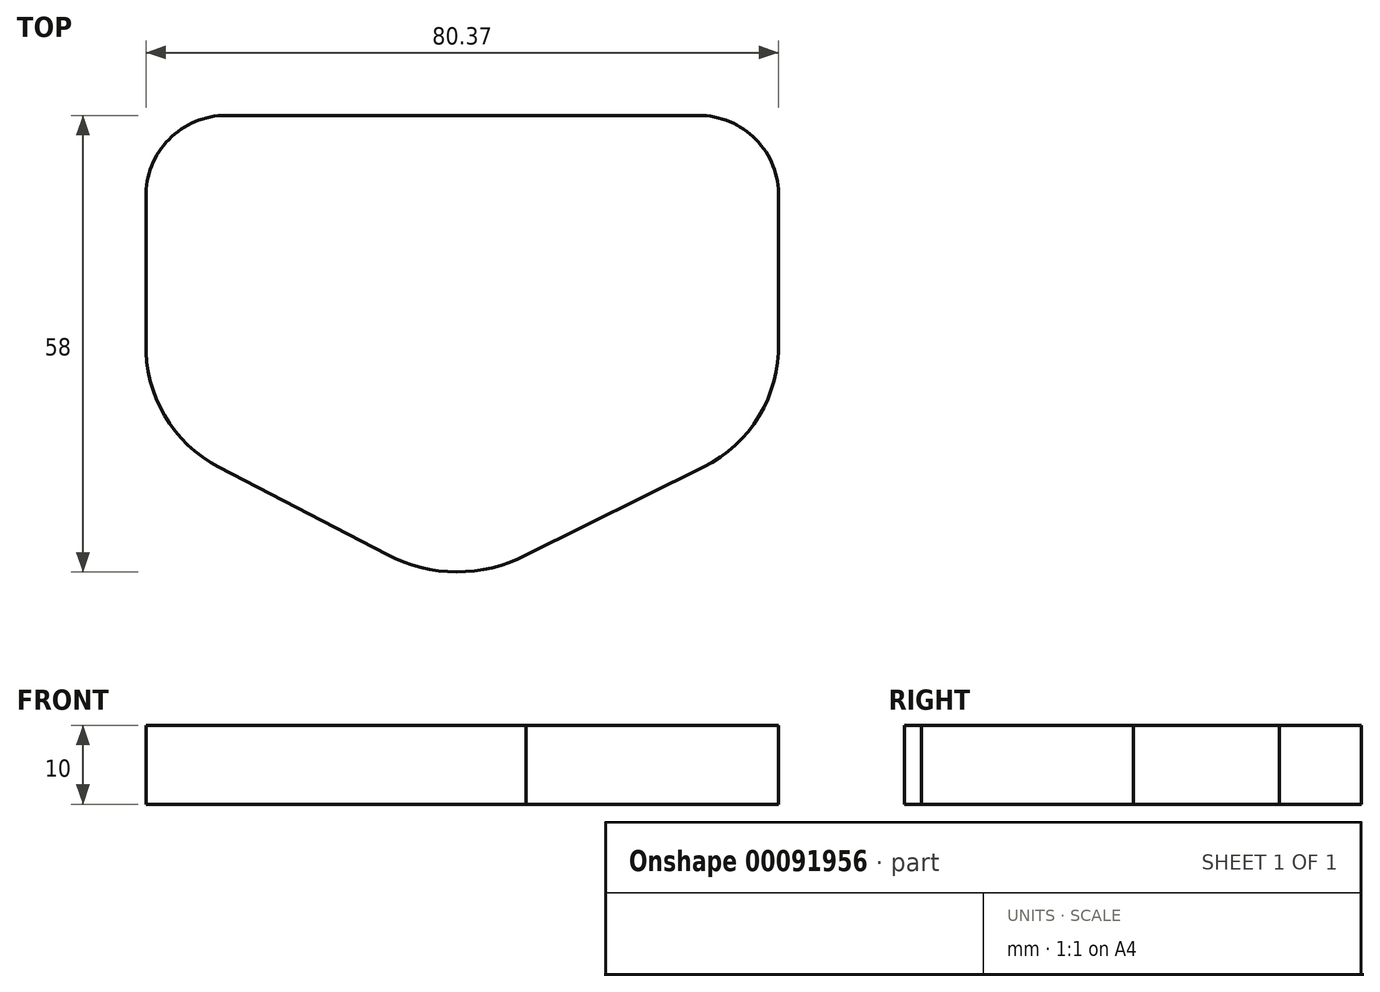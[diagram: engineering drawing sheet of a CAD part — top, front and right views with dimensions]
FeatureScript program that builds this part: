
annotation { "Feature Type Name" : "Feature", "Feature Type Description" : "" }
export const myFeature = defineFeature(function(context is Context, id is Id, definition is map)
    precondition{}
    {
        {
            var Q0;
            Q0=qCreatedBy(makeId("Top.planeOp"),FACE);
            var sketch = newSketch(context, id + "F0", { "sketchPlane" : qUnion([Q0])});
            skLineSegment(sketch, "E0.bottom", {"start": v(40, -20) * mm, "end": v(-40, -20) * mm});
            skLineSegment(sketch, "E0.top", {"start": v(30.2, 20) * mm, "end": v(-29.85, 20) * mm});
            skPoint(sketch, "E0.middle", {"position": v(0, 0) * mm});
            skPoint(sketch, "E1.visualSharp", {"position": v(-40, 20) * mm});
            skArc(sketch, "E1.filletArc", {"start": v(-29.85, 20) * mm, "mid": v(-37.1, 16.95) * mm, "end": v(-40, 9.63) * mm});
            skPoint(sketch, "E2.visualSharp", {"position": v(40, 20) * mm});
            skArc(sketch, "E2.filletArc", {"start": v(40.35, 9.63) * mm, "mid": v(37.45, 16.95) * mm, "end": v(30.2, 20) * mm});
            skPoint(sketch, "E3.visualSharp", {"position": v(0, -40.97) * mm});
            skArc(sketch, "E3.filletArc", {"start": v(-9.4, -35.78) * mm, "mid": v(-0.57, -38) * mm, "end": v(8.28, -35.87) * mm});
            skLineSegment(sketch, "E4", {"start": v(-30.76, -24.68) * mm, "end": v(-9.4, -35.78) * mm});
            skLineSegment(sketch, "E5", {"start": v(8.28, -35.87) * mm, "end": v(30.82, -24.68) * mm});
            skArc(sketch, "E6", {"start": v(-40, -8.91) * mm, "mid": v(-37.66, -18.13) * mm, "end": v(-30.76, -24.68) * mm});
            skArc(sketch, "E7", {"start": v(30.82, -24.68) * mm, "mid": v(37.88, -18.18) * mm, "end": v(40.35, -8.91) * mm});
            skLineSegment(sketch, "E8", {"start": v(40.35, -8.91) * mm, "end": v(40.35, 9.63) * mm});
            skLineSegment(sketch, "E9", {"start": v(-40, -8.91) * mm, "end": v(-40, 9.63) * mm});
            skSolve(sketch);
        }
        {
            var Q0;
            Q0=makeQuery(id+"F0.imprint","IMPRINT",FACE,{"disambiguationData":[TD([[makeQuery(id+"F0.imprint","IMPRINT",EDGE,{"derivedFrom":sQuery(id+"F0.wireOp",EDGE,"E3.filletArc")}),1.0]])]});
            var Q1;
            Q1=makeQuery(id+"F0.imprint","IMPRINT",FACE,{"disambiguationData":[TD([[makeQuery(id+"F0.imprint","IMPRINT",EDGE,{"derivedFrom":sQuery(id+"F0.wireOp",EDGE,"E0.top")}),1.0]])]});
            extrude(context, id + "F1", {"entities" : qUnion([Q0, Q1]), "depth" : 10 * mm});
        }
        {
            var Q0;
            Q0=makeQuery(id+"F1.opExtrude","CAP_FACE",FACE,{"disambiguationData":[OSD([sQuery(id+"F0.wireOp",EDGE,"E0.top"),sQuery(id+"F0.wireOp",EDGE,"E1.filletArc"),sQuery(id+"F0.wireOp",EDGE,"E2.filletArc"),sQuery(id+"F0.wireOp",EDGE,"E3.filletArc"),sQuery(id+"F0.wireOp",EDGE,"E4"),sQuery(id+"F0.wireOp",EDGE,"E5"),sQuery(id+"F0.wireOp",EDGE,"E6"),sQuery(id+"F0.wireOp",EDGE,"E7"),sQuery(id+"F0.wireOp",EDGE,"E8"),sQuery(id+"F0.wireOp",EDGE,"E9")])],"isStart":false});
            cPlane(context, id + "F2", {"entities" : qUnion([Q0]), "cplaneType" : CPlaneType.OFFSET, "offset" : 15 * mm, "width" : 152.4 * mm, "height" : 152.4 * mm});
        }
    });
